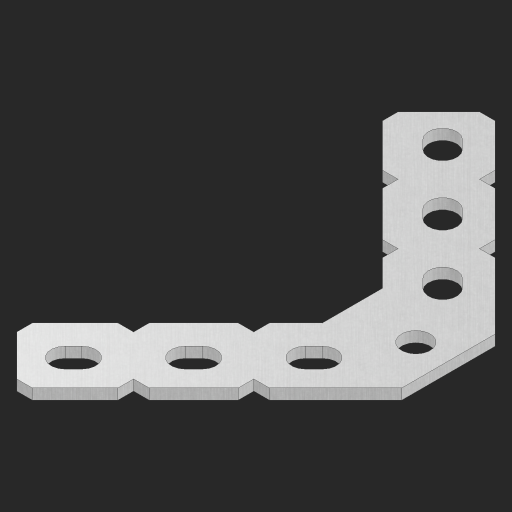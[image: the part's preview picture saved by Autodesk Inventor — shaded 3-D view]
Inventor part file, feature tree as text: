
AUTODESK INVENTOR PART (.ipt)
format: ipt  version: 2023 (Build 270158000, 158)  size: 245,760 bytes
history: native  units: in
note: dims shown in document units (in); Inventor stores cm internally (conversion verified against a paired STEP export)
features: chamfer x1, other x1, imported_body x1
ambient origin geometry x8: Origin, YZ Plane, XZ Plane, XY Plane, X Axis, Y Axis, Z Axis, Center Point
bodies: Body1 (feature_tree)
feature tree (3):
  chamfer  "Chamfer1"  [1 undecoded]
  other  "90-Degree Gusset Plate"
  imported_body  "Base1"
note: 1 required parameter value undecoded (feature->parameter linkage not recoverable at this tier; creation-order binding heuristic only, values carry confidence <= 0.55)
